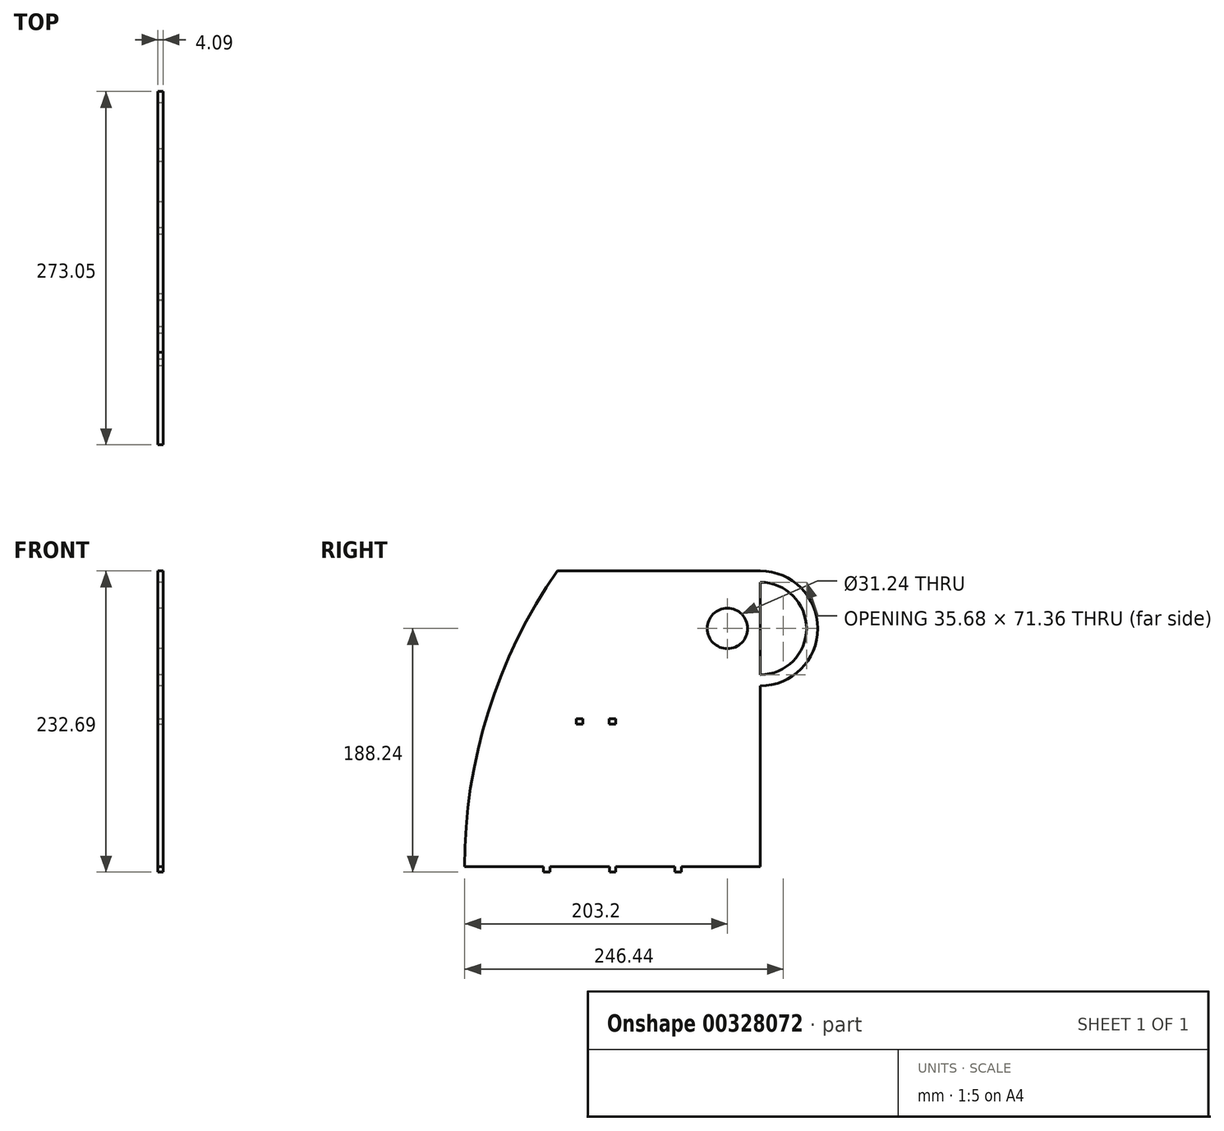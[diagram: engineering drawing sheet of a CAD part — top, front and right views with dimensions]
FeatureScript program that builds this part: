
annotation { "Feature Type Name" : "Feature", "Feature Type Description" : "" }
export const myFeature = defineFeature(function(context is Context, id is Id, definition is map)
    precondition{}
    {
        {
            var Q0;
            Q0=qCreatedBy(makeId("Right.planeOp"),FACE);
            var sketch = newSketch(context, id + "F0", { "sketchPlane" : qUnion([Q0])});
            skLineSegment(sketch, "E0.bottom", {"start": v(114.3, -139.7) * mm, "end": v(-114.3, -139.7) * mm});
            skLineSegment(sketch, "E0.left", {"start": v(114.3, -139.7) * mm, "end": v(114.3, 88.9) * mm});
            skPoint(sketch, "E0.middle", {"position": v(0, 0) * mm});
            skArc(sketch, "E1", {"start": v(-42.67, 88.9) * mm, "mid": v(-96.06, -19.9) * mm, "end": v(-114.3, -139.7) * mm});
            skLineSegment(sketch, "E2", {"start": v(-42.67, 88.9) * mm, "end": v(114.3, 88.9) * mm});
            skLineSegment(sketch, "E3", {"start": v(0, -139.7) * mm, "end": v(0, 44.45) * mm, "construction": true});
            skLineSegment(sketch, "E4", {"start": v(0, 44.45) * mm, "end": v(88.9, 44.45) * mm, "construction": true});
            skCircle(sketch, "E5", {"center": v(88.9, 44.45) * mm, "radius": 15.62 * mm});
            skArc(sketch, "E6", {"start": v(114.3, 0) * mm, "mid": v(158.75, 44.45) * mm, "end": v(114.3, 88.9) * mm});
            skArc(sketch, "E7.trimOffspring", {"start": v(114.3, 8.77) * mm, "mid": v(149.98, 44.45) * mm, "end": v(114.3, 80.13) * mm});
            skLineSegment(sketch, "E8.left", {"start": v(2.41, -139.7) * mm, "end": v(2.41, -143.79) * mm});
            skLineSegment(sketch, "E8.right", {"start": v(-2.41, -139.7) * mm, "end": v(-2.41, -143.79) * mm});
            skPoint(sketch, "E8.middle", {"position": v(0, -139.7) * mm});
            skPoint(sketch, "E9.orphan", {"position": v(-2.41, -132.4) * mm});
            skPoint(sketch, "E10.orphan", {"position": v(2.41, -132.4) * mm});
            skLineSegment(sketch, "E11", {"start": v(-2.41, -143.79) * mm, "end": v(2.41, -143.79) * mm});
            skPoint(sketch, "E8.top.end.orphan", {"position": v(-2.41, -147) * mm});
            skPoint(sketch, "E12.orphan", {"position": v(2.41, -147) * mm});
            skLineSegment(sketch, "E13", {"start": v(0, -139.7) * mm, "end": v(50.8, -139.7) * mm, "construction": true});
            skLineSegment(sketch, "E14.bottom", {"start": v(48.26, -143.79) * mm, "end": v(53.34, -143.79) * mm});
            skLineSegment(sketch, "E14.left", {"start": v(48.26, -143.79) * mm, "end": v(48.26, -139.7) * mm});
            skLineSegment(sketch, "E14.right", {"start": v(53.34, -143.79) * mm, "end": v(53.34, -139.7) * mm});
            skPoint(sketch, "E14.middle", {"position": v(50.8, -139.7) * mm});
            skLineSegment(sketch, "E15", {"start": v(0, -139.7) * mm, "end": v(-50.8, -139.7) * mm, "construction": true});
            skPoint(sketch, "E16.middle", {"position": v(-50.8, -139.7) * mm});
            skPoint(sketch, "E16.bottom.start.orphan", {"position": v(-53.34, -132.64) * mm});
            skPoint(sketch, "E17.orphan", {"position": v(-48.26, -132.64) * mm});
            skLineSegment(sketch, "E18.bottom", {"start": v(-48.26, -143.79) * mm, "end": v(-53.34, -143.79) * mm});
            skLineSegment(sketch, "E18.left", {"start": v(-48.26, -143.79) * mm, "end": v(-48.26, -139.7) * mm});
            skLineSegment(sketch, "E18.right", {"start": v(-53.34, -143.79) * mm, "end": v(-53.34, -139.7) * mm});
            skPoint(sketch, "E18.top.end.orphan", {"position": v(-53.34, -135.61) * mm});
            skPoint(sketch, "E19.orphan", {"position": v(-48.26, -135.61) * mm});
            skPoint(sketch, "E14.top.start.orphan", {"position": v(48.26, -135.61) * mm});
            skPoint(sketch, "E20.orphan", {"position": v(53.34, -135.61) * mm});
            skSolve(sketch);
        }
        {
            var Q0;
            Q0 = qSketchRegion(id + "F0", true);
            extrude(context, id + "F1", {"entities" : qUnion([Q0]), "depth" : 4.1 * mm});
        }
        {
            var Q0;
            Q0=makeQuery(id+"F1.opExtrude","CAP_FACE",FACE,{"disambiguationData":[OSD([sQuery(id+"F0.wireOp",EDGE,"E0.bottom"),sQuery(id+"F0.wireOp",EDGE,"E0.left"),sQuery(id+"F0.wireOp",EDGE,"E1"),sQuery(id+"F0.wireOp",EDGE,"E2"),sQuery(id+"F0.wireOp",EDGE,"E5"),sQuery(id+"F0.wireOp",EDGE,"E6"),sQuery(id+"F0.wireOp",EDGE,"E7.trimOffspring"),sQuery(id+"F0.wireOp",EDGE,"E8.left"),sQuery(id+"F0.wireOp",EDGE,"E8.right"),sQuery(id+"F0.wireOp",EDGE,"E11"),sQuery(id+"F0.wireOp",EDGE,"E14.bottom"),sQuery(id+"F0.wireOp",EDGE,"E14.left"),sQuery(id+"F0.wireOp",EDGE,"E14.right"),sQuery(id+"F0.wireOp",EDGE,"E18.bottom"),sQuery(id+"F0.wireOp",EDGE,"E18.left"),sQuery(id+"F0.wireOp",EDGE,"E18.right")])],"isStart":false});
            var sketch = newSketch(context, id + "F2", { "sketchPlane" : qUnion([Q0])});
            skLineSegment(sketch, "E21", {"start": v(0, -143.79) * mm, "end": v(0, 88.9) * mm, "construction": true});
            skLineSegment(sketch, "E22", {"start": v(0, -27.44) * mm, "end": v(-25.4, -27.44) * mm, "construction": true});
            skPoint(sketch, "E22.endSnap0", {"position": v(0, -27.44) * mm});
            skLineSegment(sketch, "E23.bottom", {"start": v(2.54, -29.49) * mm, "end": v(-2.54, -29.49) * mm});
            skLineSegment(sketch, "E23.top", {"start": v(2.54, -25.4) * mm, "end": v(-2.54, -25.4) * mm});
            skLineSegment(sketch, "E23.left", {"start": v(2.54, -29.49) * mm, "end": v(2.54, -25.4) * mm});
            skLineSegment(sketch, "E23.right", {"start": v(-2.54, -29.49) * mm, "end": v(-2.54, -25.4) * mm});
            skLineSegment(sketch, "E24.bottom", {"start": v(-22.86, -29.49) * mm, "end": v(-27.94, -29.49) * mm});
            skLineSegment(sketch, "E24.top", {"start": v(-22.86, -25.4) * mm, "end": v(-27.94, -25.4) * mm});
            skLineSegment(sketch, "E24.left", {"start": v(-22.86, -29.49) * mm, "end": v(-22.86, -25.4) * mm});
            skLineSegment(sketch, "E24.right", {"start": v(-27.94, -29.49) * mm, "end": v(-27.94, -25.4) * mm});
            skPoint(sketch, "E24.middle", {"position": v(-25.4, -27.44) * mm});
            skSolve(sketch);
        }
        {
            var Q0;
            Q0 = qSketchRegion(id + "F2", true);
            extrude(context, id + "F3", {"entities" : qUnion([Q0]), "operationType" : NewBodyOperationType.REMOVE, "oppositeDirection" : true, "depth" : 25.4 * mm});
        }
    });
